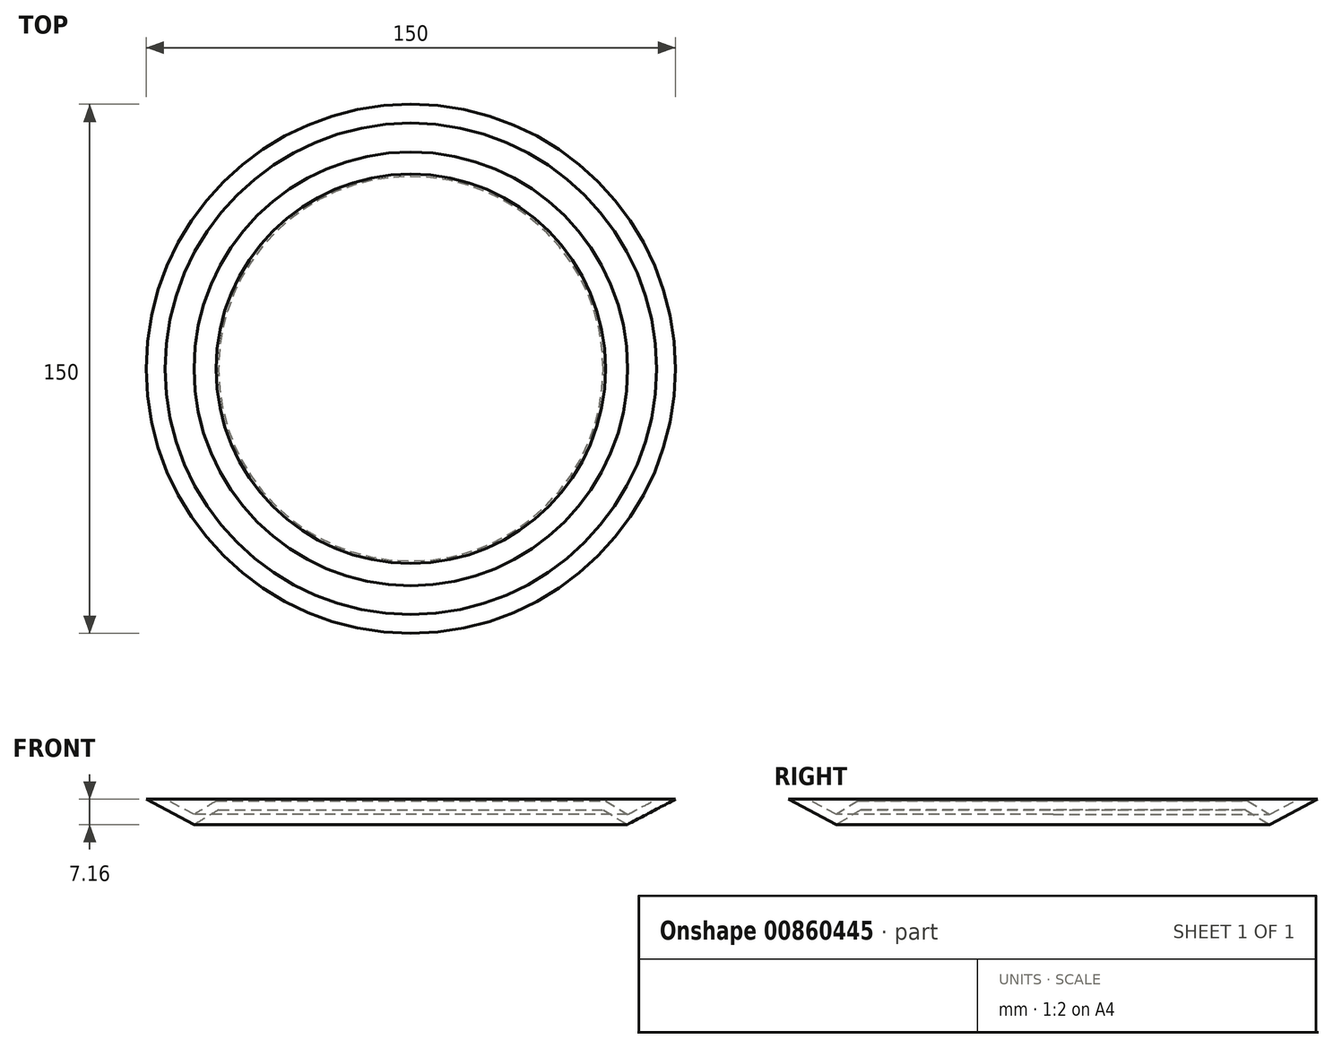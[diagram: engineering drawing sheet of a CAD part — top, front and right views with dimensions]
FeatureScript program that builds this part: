
annotation { "Feature Type Name" : "Feature", "Feature Type Description" : "" }
export const myFeature = defineFeature(function(context is Context, id is Id, definition is map)
    precondition{}
    {
        {
            var Q0;
            Q0=qCreatedBy(makeId("Top.planeOp"),FACE);
            var sketch = newSketch(context, id + "F0", { "sketchPlane" : qUnion([Q0])});
            skCircle(sketch, "E0", {"center": v(0, 0) * mm, "radius": 35 * mm});
            skSolve(sketch);
        }
        {
            var Q0;
            Q0=qCreatedBy(makeId("Top.planeOp"),FACE);
            cPlane(context, id + "F1", {"entities" : qUnion([Q0]), "cplaneType" : CPlaneType.OFFSET, "offset" : 21 * mm, "width" : 150 * mm, "height" : 150 * mm});
        }
        {
            var Q0;
            Q0=qCreatedBy(id+"F1.planeOp",FACE);
            var sketch = newSketch(context, id + "F2", { "sketchPlane" : qUnion([Q0])});
            skCircle(sketch, "E1", {"center": v(0, 0) * mm, "radius": 75 * mm});
            skCircle(sketch, "E2.0", {"center": v(0, 0) * mm, "radius": 35 * mm, "construction": true});
            skSolve(sketch);
        }
        {
            var Q0;
            Q0=makeQuery(id+"F0.imprint","IMPRINT",FACE,{"disambiguationData":[TD([[makeQuery(id+"F0.imprint","IMPRINT",EDGE,{"derivedFrom":sQuery(id+"F0.wireOp",EDGE,"E0")}),1.0]])]});
            var Q1;
            Q1=makeQuery(id+"F2.imprint","IMPRINT",FACE,{"disambiguationData":[TD([[makeQuery(id+"F2.imprint","IMPRINT",EDGE,{"derivedFrom":sQuery(id+"F2.wireOp",EDGE,"E1")}),1.0]])]});
            loft(context, id + "F3", {"sheetProfilesArray" : [{ "sheetProfileEntities" : qUnion([Q0]) }, { "sheetProfileEntities" : qUnion([Q1]) }]});
        }
        {
            var Q0;
            Q0=makeQuery(id+"F3.opLoft","CAP_FACE",FACE,{"disambiguationData":[OSD([makeQuery(id+"F0.imprint","IMPRINT",FACE,{"disambiguationData":[TD([[makeQuery(id+"F0.imprint","IMPRINT",EDGE,{"derivedFrom":sQuery(id+"F0.wireOp",EDGE,"E0")}),1.0]])]})])],"isStart":true});
            var sketch = newSketch(context, id + "F4", { "sketchPlane" : qUnion([Q0])});
            skCircle(sketch, "E3.0", {"center": v(0, 0) * mm, "radius": 35 * mm});
            skSolve(sketch);
        }
        {
            var Q0;
            Q0 = qSketchRegion(id + "F4", true);
            extrude(context, id + "F5", {"entities" : qUnion([Q0]), "operationType" : NewBodyOperationType.REMOVE, "oppositeDirection" : true, "depth" : 18 * mm, "offsetDistance" : 25 * mm});
        }
        {
            var Q0;
            Q0=makeQuery(id+"F5.boolean.opBoolean","MERGE",EDGE,{"derivedFrom":[makeQuery(id+"F3.opLoft","MID_CAP_EDGE",EDGE,{"disambiguationData":[OSD([sQuery(id+"F0.wireOp",EDGE,"E0")])],"capPos":0.0}),makeQuery(id+"F5.opExtrude","CAP_EDGE",EDGE,{"disambiguationData":[OSD([sQuery(id+"F4.wireOp",EDGE,"E3.0")])],"isStart":true})]});
            chamfer(context, id + "F6", {"entities" : qUnion([Q0]), "width" : 18 * mm, "tangentPropagation" : true});
        }
        {
            var Q0;
            Q0=makeQuery(id+"F3.opLoft","CAP_FACE",FACE,{"disambiguationData":[OSD([makeQuery(id+"F2.imprint","IMPRINT",FACE,{"disambiguationData":[TD([[makeQuery(id+"F2.imprint","IMPRINT",EDGE,{"derivedFrom":sQuery(id+"F2.wireOp",EDGE,"E1")}),1.0]])]})])],"isStart":true});
            shell(context, id + "F7", {"entities" : qUnion([Q0]), "thickness" : 2.5 * mm});
        }
    });
